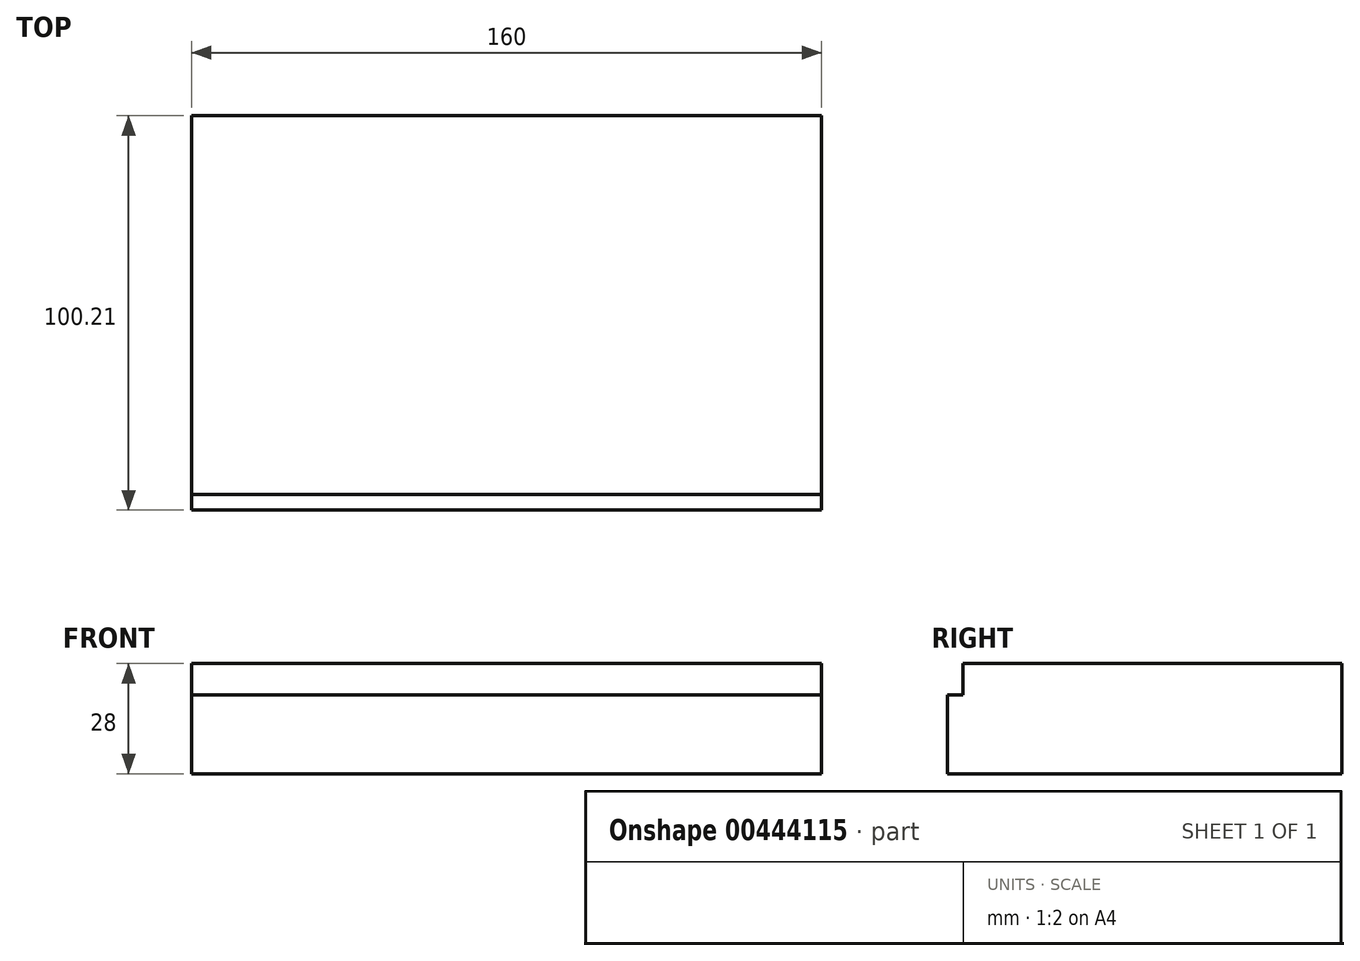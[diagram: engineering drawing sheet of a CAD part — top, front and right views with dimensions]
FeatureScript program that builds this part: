
annotation { "Feature Type Name" : "Feature", "Feature Type Description" : "" }
export const myFeature = defineFeature(function(context is Context, id is Id, definition is map)
    precondition{}
    {
        {
            var Q0;
            Q0=qCreatedBy(makeId("Top.planeOp"),FACE);
            var sketch = newSketch(context, id + "F0", { "sketchPlane" : qUnion([Q0])});
            skLineSegment(sketch, "E0.bottom", {"start": v(-111.15, 57.28) * mm, "end": v(88.85, 57.28) * mm});
            skLineSegment(sketch, "E0.top", {"start": v(-111.15, -54.93) * mm, "end": v(88.85, -54.93) * mm});
            skLineSegment(sketch, "E0.left", {"start": v(-111.15, 57.28) * mm, "end": v(-111.15, -54.93) * mm});
            skLineSegment(sketch, "E0.right", {"start": v(88.85, 57.28) * mm, "end": v(88.85, -54.93) * mm});
            skLineSegment(sketch, "E1.bottom", {"start": v(-111.15, 57.28) * mm, "end": v(-91.15, 57.28) * mm});
            skLineSegment(sketch, "E1.top", {"start": v(-111.15, -54.93) * mm, "end": v(-91.15, -54.93) * mm});
            skLineSegment(sketch, "E1.right", {"start": v(-91.15, 57.28) * mm, "end": v(-91.15, -54.93) * mm});
            skLineSegment(sketch, "E2.bottom", {"start": v(88.85, 57.28) * mm, "end": v(68.85, 57.28) * mm});
            skLineSegment(sketch, "E2.top", {"start": v(88.85, -54.93) * mm, "end": v(68.85, -54.93) * mm});
            skLineSegment(sketch, "E2.right", {"start": v(68.85, 57.28) * mm, "end": v(68.85, -54.93) * mm});
            skLineSegment(sketch, "E3.bottom", {"start": v(-91.15, 57.28) * mm, "end": v(68.85, 57.28) * mm});
            skLineSegment(sketch, "E3.top", {"start": v(-91.15, 49.28) * mm, "end": v(68.85, 49.28) * mm});
            skLineSegment(sketch, "E3.left", {"start": v(-91.15, 57.28) * mm, "end": v(-91.15, 49.28) * mm});
            skLineSegment(sketch, "E3.right", {"start": v(68.85, 57.28) * mm, "end": v(68.85, 49.28) * mm});
            skLineSegment(sketch, "E4.top", {"start": v(-91.15, 45.28) * mm, "end": v(68.85, 45.28) * mm});
            skLineSegment(sketch, "E4.left", {"start": v(-91.15, 49.28) * mm, "end": v(-91.15, 45.28) * mm});
            skLineSegment(sketch, "E4.right", {"start": v(68.85, 49.28) * mm, "end": v(68.85, 45.28) * mm});
            skLineSegment(sketch, "E5.top", {"start": v(-91.15, -50.93) * mm, "end": v(68.85, -50.93) * mm});
            skLineSegment(sketch, "E5.left", {"start": v(-91.15, 45.28) * mm, "end": v(-91.15, -50.93) * mm});
            skLineSegment(sketch, "E5.right", {"start": v(68.85, 45.28) * mm, "end": v(68.85, -50.93) * mm});
            skLineSegment(sketch, "E6.top", {"start": v(-91.15, -54.93) * mm, "end": v(68.85, -54.93) * mm});
            skLineSegment(sketch, "E6.left", {"start": v(-91.15, -50.93) * mm, "end": v(-91.15, -54.93) * mm});
            skLineSegment(sketch, "E6.right", {"start": v(68.85, -50.93) * mm, "end": v(68.85, -54.93) * mm});
            skSolve(sketch);
        }
        {
            var Q0;
            Q0=makeQuery(id+"F0.imprint","IMPRINT",FACE,{"disambiguationData":[TD([[makeQuery(id+"F0.imprint","IMPRINT",EDGE,{"derivedFrom":sQuery(id+"F0.wireOp",EDGE,"E1.bottom")}),-1.0]])]});
            var Q1;
            Q1=makeQuery(id+"F0.imprint","IMPRINT",FACE,{"disambiguationData":[TD([[makeQuery(id+"F0.imprint","IMPRINT",EDGE,{"derivedFrom":sQuery(id+"F0.wireOp",EDGE,"E2.bottom")}),1.0]])]});
            var Q2;
            Q2=makeQuery(id+"F0.imprint","IMPRINT",FACE,{"disambiguationData":[TD([[makeQuery(id+"F0.imprint","IMPRINT",EDGE,{"derivedFrom":sQuery(id+"F0.wireOp",EDGE,"E4.left")}),1.0]])]});
            var Q3;
            Q3=makeQuery(id+"F0.imprint","IMPRINT",FACE,{"disambiguationData":[TD([[makeQuery(id+"F0.imprint","IMPRINT",EDGE,{"derivedFrom":sQuery(id+"F0.wireOp",EDGE,"E5.top")}),-1.0]])]});
            extrude(context, id + "F1", {"entities" : qUnion([Q0, Q1, Q2, Q3]), "depth" : 20 * mm});
        }
        {
            var Q0;
            Q0=makeQuery(id+"F0.imprint","IMPRINT",FACE,{"disambiguationData":[TD([[makeQuery(id+"F0.imprint","IMPRINT",EDGE,{"derivedFrom":sQuery(id+"F0.wireOp",EDGE,"E3.bottom")}),-1.0]])]});
            var Q1;
            Q1=makeQuery(id+"F0.imprint","IMPRINT",FACE,{"disambiguationData":[TD([[makeQuery(id+"F0.imprint","IMPRINT",EDGE,{"derivedFrom":sQuery(id+"F0.wireOp",EDGE,"E4.top")}),-1.0]])]});
            extrude(context, id + "F2", {"entities" : qUnion([Q0, Q1]), "operationType" : NewBodyOperationType.ADD, "depth" : 28 * mm});
        }
    });
